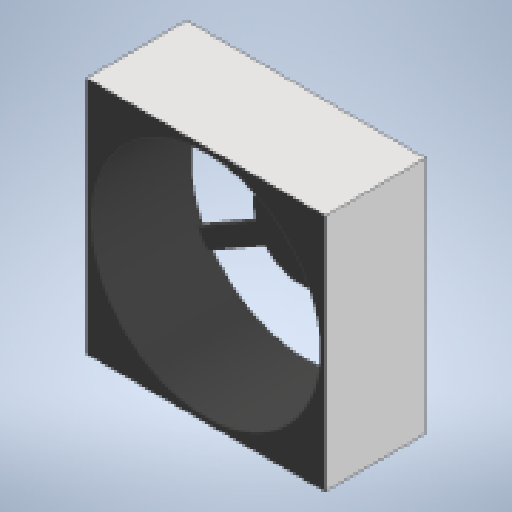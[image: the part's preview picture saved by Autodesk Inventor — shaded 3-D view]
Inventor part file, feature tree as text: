
AUTODESK INVENTOR PART (.ipt)
format: ipt  version: 2023.1 (Build 271208000, 208)  size: 248,320 bytes
history: native  units: mm
features: extrude x3, sketch x3, other x1
ambient origin geometry x8: Origin, YZ Plane, XZ Plane, XY Plane, X Axis, Y Axis, Z Axis, Center Point
bodies: Body1 (feature_tree)
feature tree (7):
  other  "솔리드1"
  extrude  "돌출1"  Depth=25.0mm
  extrude  "돌출2"  Depth=25.0mm
  extrude  "돌출3"  Depth=10.5mm TaperAngle=0.0deg
  sketch  "스케치1"
  sketch  "스케치2"
  sketch  "스케치3"
